# Revit family: IS_Iom_A9104_BIM_IT
name_source: partatom
category: Furniture
revit_build: Autodesk Revit 2017 (Build: 20160225_1515(x64)
units: mm (PartAtom-declared; Revit-internal decimal feet)

## family parameters
Always vertical = No
Cut with Voids When Loaded = No
OmniClass Number = 23.45.05.00
OmniClass Title = Sanitary Equipment
Room Calculation Point = No
Shared = No
Work Plane-Based = No

## types (1)
- A9104MY - IOM WST BIN POL S/S PEDAL 3L
    AltezzaNominale = 0 mm  [stored 0 ft]
    BIMobject category = Accessories
    BIMobject category code = sanitary-accessories1
    BIMobject main category = Sanitary
    BIMobject main category code = sanitary
    BOSUseNativeGeometries = 1
    Brand url = http://www.idealstandard.co.uk
    CostoDiSostituzione = 0 $
    DimensioneScarico = 0
    EAN code = https://4015413328111
    Edition number = 1
    IFC Classification = Sanitary Terminal
    Installation instructions = http://www.idealstandard.it
    LarghezzaNominale = 0 mm  [stored 0 ft]
    LunghezzaNominale = 0 mm  [stored 0 ft]
    Maniglia = No
    Manufacturer name = Ideal Standard
    Model = A9104MY
    NBS Reference Code = 35-76-80
    NBS Reference Description = Soap Dispensers
    Nominal depth = 0
    Nominal height = 0
    NominalHeight = 257 mm
    NominalLength = 236 mm
    NominalWidth = 174 mm
    OmniClass Code = 23-31 25 00
    OmniClass Description = Toilet and Bath Specialties
    PiattoDoccia = No
    Product Guid = fc2c962d-5686-4390-a5ab-86f5ff4ca98a
    Product SKU = A9104
    Product certification = http://www.idealstandard.it
    Product data url = https://bimobject.com
    Product family = Sanitary
    Product group = Soap Dispensers
    Product name = IOM WST BIN POL S/S PEDAL 3L
    Product url = http://www.idealstandard.it
    ProfonditaNominale = 0 mm  [stored 0 ft]
    QR code = http://bimobject.com
    SeatMaterial = 0 mm  [stored 0 ft]
    Size = 257 x 236 x 174mm
    SpessoreDelMateriale = 0
    SpilloverLivello = 0
    Technical description = http://www.idealstandard.it
    Uniclass 2.0 Code = PR-35-76-80
    Uniclass 2.0 Description = Soap Dispensers
    Uniclass 2015 Code = Pr_40_70_22_81
    Uniclass 2015 Name = Soap dispensers
    Weight Net (Kg) = 0

note: [stored X ft] marks values corroborated as IEEE doubles in the binary element streams (Revit-internal decimal feet)

## geometry (parser evidence)
native form markers: Sweep x3
no freeform markers — native parametric forms only
